# Revit family: Kühltische GN2-3 - Eigen
name_source: partatom
category: Sonderausstattung
revit_build: Autodesk Revit MEP 2015 (Build: 20140606_1530(x64)
units: mm (PartAtom-declared; Revit-internal decimal feet)

## types (4) — shared parameters
Abstand Display seitlich = 60 mm  [stored 0.19685 ft]
Artnr mit Platte = KTM 622342
Artnr mit Platte und Aufkantung = KTM 622341
Artnr ohne Platte = KTM 622340
Aufkantung Stärke = 6 mm  [stored 0.019685 ft]
Energieverbrauch = 2,5 kWh/24 h
Höhe Elektroanschluss = 150 mm
Kapazität = 2 x 6 x GN2/3
Korpus Tiefe = 520 mm  [stored 1.70604 ft]
Kälteleistung = 380 Watt -15°C VT/+32°C UT
Kältemittel = R134a
Material = Edelstahl AISI 304
Pfosten 1 = Ja
Pfosten Breite = 100 mm  [stored 0.328084 ft]
Pfosten Tiefe = 50 mm  [stored 0.164042 ft]
Platte Tiefe = 600 mm
Pole = 1
Rückwand Stärke = 50 mm  [stored 0.164042 ft]
Scheinleistung = 0 VA
Seitenteil Breite = 320 mm  [stored 1.04987 ft]
Seitenteilwand Stärke = 15 mm  [stored 0.0492126 ft]
Seitenwand Stärke = 50 mm  [stored 0.164042 ft]
Sockelhöhe = 150 mm
Spannung = 230 V
Temp. Bereich = -2°C bis +10°C
Tür_1 = Ja
Tür_2 = Ja
Türen Breite = 430 mm  [stored 1.41076 ft]
Türen Breite halb = 215 mm  [stored 0.705381 ft]
Türen Stärke = 50 mm  [stored 0.164042 ft]
Wand oben Stärke = 50 mm  [stored 0.164042 ft]
Wand unten Stärke = 50 mm  [stored 0.164042 ft]
Öffnungstiefe = 370 mm  [stored 1.21391 ft]

## per-type parameters (varying)
| type | Abstand Logo | Aufkantung Höhe | Breite | Korpus Breite | Korpus Höhe | Pfosten 2 | Pfosten Abstand | Pfosten Anzahl | Platte Stärke | Tür_3 | Türen Anzahl | Türen Höhe | Türen Lücke | Versatz Tür zu Seitenteil | Watt |
| 435x1250 2-türig | 158 mm | 20 mm  [stored 0.0656168 ft] | 1250 mm  [stored 4.10105 ft] | 915 mm | 435 mm  [stored 1.42717 ft] | Nein | 440 mm | 1 | 20 mm  [stored 0.0656168 ft] | Nein | 2 | 415 mm  [stored 1.36155 ft] | 20 mm  [stored 0.0656168 ft] | 20 mm  [stored 0.0656168 ft] | 440 W |
| 435x1725 3-türig | 158 mm | 20 mm  [stored 0.0656168 ft] | 1725 mm | 1390 mm | 435 mm  [stored 1.42717 ft] | Ja | 445 mm | 2 | 20 mm  [stored 0.0656168 ft] | Ja | 3 | 415 mm  [stored 1.36155 ft] | 30 mm  [stored 0.0984252 ft] | 25 mm  [stored 0.082021 ft] | 460 W |
| 650x1250 2-türig | 265 mm | 50 mm  [stored 0.164042 ft] | 1250 mm  [stored 4.10105 ft] | 915 mm | 650 mm | Nein | 440 mm | 1 | 50 mm  [stored 0.164042 ft] | Nein | 2 | 630 mm  [stored 2.06693 ft] | 20 mm  [stored 0.0656168 ft] | 20 mm  [stored 0.0656168 ft] | 440 W |
| 650x1725 3-türig | 265 mm | 50 mm  [stored 0.164042 ft] | 1725 mm | 1390 mm | 650 mm | Ja | 445 mm | 2 | 50 mm  [stored 0.164042 ft] | Ja | 3 | 630 mm  [stored 2.06693 ft] | 30 mm  [stored 0.0984252 ft] | 25 mm  [stored 0.082021 ft] | 460 W |

note: [stored X ft] marks values corroborated as IEEE doubles in the binary element streams (Revit-internal decimal feet)

## geometry (parser evidence)
native form markers: Blend x15, Sweep x6
no freeform markers — native parametric forms only
